# Revit family: LC-4
name_source: partatom
category: Generic Models
revit_build: Autodesk Revit 2017 (Build: 20170419_0315(x64)
units: mm (PartAtom-declared; Revit-internal decimal feet)

## family parameters
Always vertical = Yes
Can host rebar = No
Cut with Voids When Loaded = No
Host = Wall
Part Type = Normal
Room Calculation Point = No
Round Connector Dimension = Use Diameter
Shared = No

## types (3) — shared parameters
Depth = 88 mm
Height = 510 mm
Keynote = 6120
Manufacturer = Sentakia Oy
Materiaali = kromattu messinki (CuZn36As)
Sentakia_Material_Default = Steel Chrome plated_sentakia
URL = http://www.sentakia.com

## per-type parameters (varying)
| type | EAN | LVI | Leveys | Model | Teho |
| 350 | 4770046007566 | 5489939 | 350 mm | LC-4/350 | kromi: 50 W maalattu: 65 W |
| 500 | 4770046005999 | 5489940 | 500 mm | LC-4/500 | kromi: 56 W maalattu: 73 W |
| 600 | 4770046007573 | 5489941 | 600 mm | LC-4/600 | kromi: 68 W maalattu: 88 W |

## geometry (parser evidence)
native form markers: Blend x2, Sweep x2
no freeform markers — native parametric forms only
